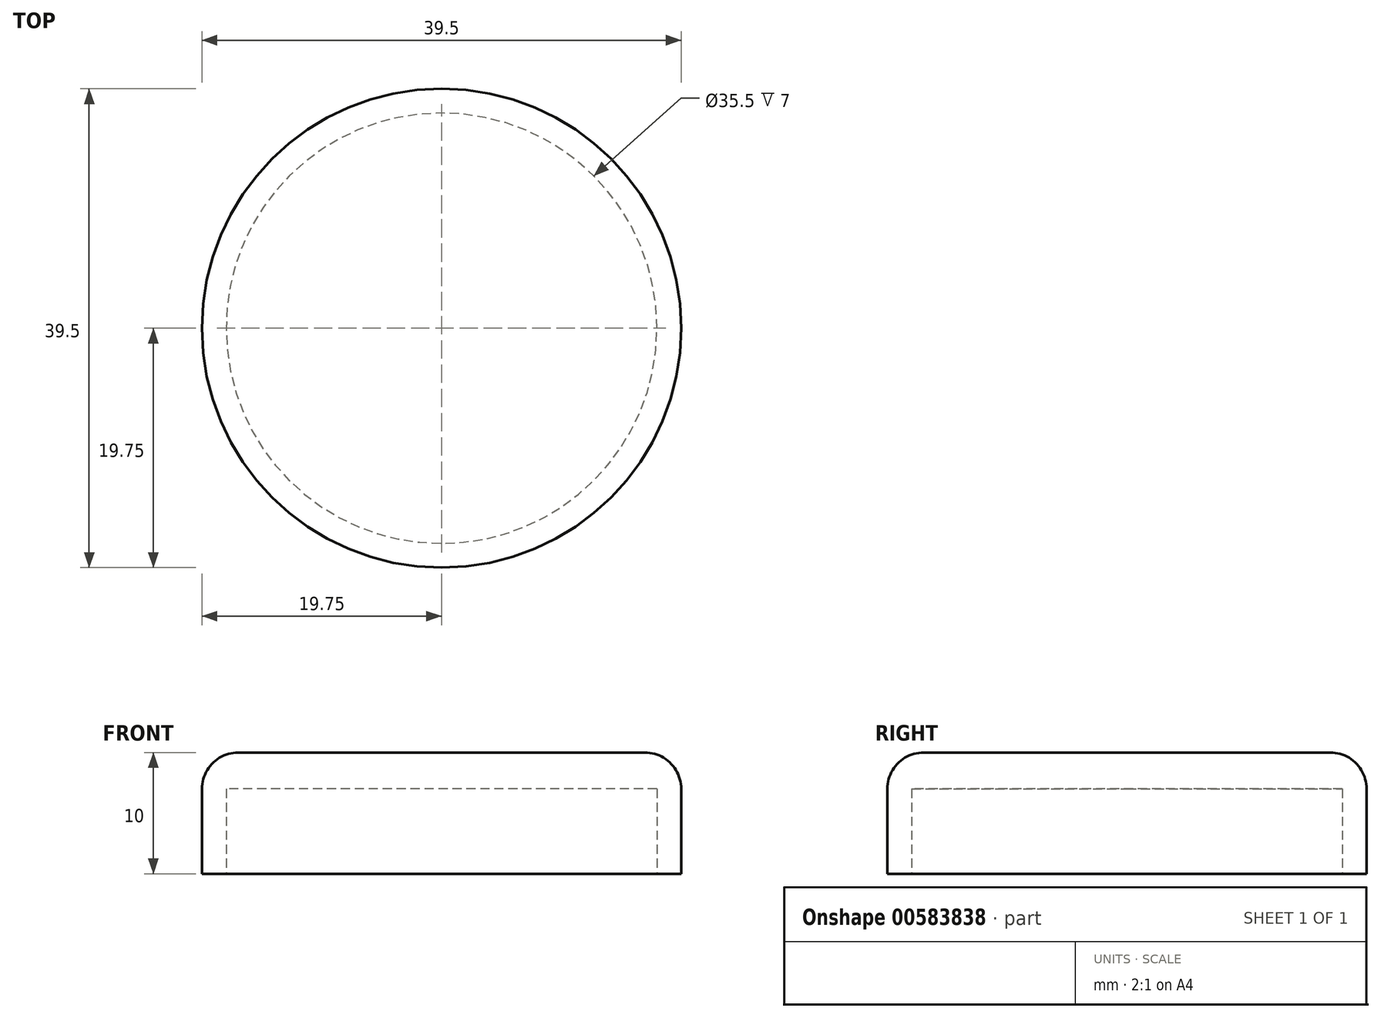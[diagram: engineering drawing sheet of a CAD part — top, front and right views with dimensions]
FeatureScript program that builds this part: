
annotation { "Feature Type Name" : "Feature", "Feature Type Description" : "" }
export const myFeature = defineFeature(function(context is Context, id is Id, definition is map)
    precondition{}
    {
        {
            assignVariable(context, id + "F0", {"name" : "OuterHeight", "anyValue" : 10});
        }
        {
            assignVariable(context, id + "F1", {"name" : "BaseDepth", "anyValue" : 3});
        }
        {
            var Q0;
            Q0=qCreatedBy(makeId("Top.planeOp"),FACE);
            var sketch = newSketch(context, id + "F2", { "sketchPlane" : qUnion([Q0])});
            skCircle(sketch, "E0", {"center": v(0, 0) * mm, "radius": 17.75 * mm});
            skCircle(sketch, "E1", {"center": v(0, 0) * mm, "radius": 19.75 * mm});
            skSolve(sketch);
        }
        {
            var Q0;
            Q0=makeQuery(id+"F2.imprint","IMPRINT",FACE,{"disambiguationData":[TD([[makeQuery(id+"F2.imprint","IMPRINT",EDGE,{"derivedFrom":sQuery(id+"F2.wireOp",EDGE,"E0")}),-1.0]])]});
            var Q1;
            Q1=makeQuery(id+"F2.imprint","IMPRINT",FACE,{"disambiguationData":[TD([[makeQuery(id+"F2.imprint","IMPRINT",EDGE,{"derivedFrom":sQuery(id+"F2.wireOp",EDGE,"E0")}),1.0]])]});
            extrude(context, id + "F3", {"entities" : qUnion([Q0, Q1]), "depth" : getVariable(context, 'OuterHeight') * mm, "offsetDistance" : 25 * mm});
        }
        {
            var Q0;
            Q0=makeQuery(id+"F2.imprint","IMPRINT",FACE,{"disambiguationData":[TD([[makeQuery(id+"F2.imprint","IMPRINT",EDGE,{"derivedFrom":sQuery(id+"F2.wireOp",EDGE,"E0")}),1.0]])]});
            extrude(context, id + "F4", {"entities" : qUnion([Q0]), "operationType" : NewBodyOperationType.REMOVE, "depth" : (getVariable(context, 'OuterHeight') - getVariable(context, 'BaseDepth')) * mm, "offsetDistance" : 25 * mm});
        }
        {
            var Q0;
            Q0=makeQuery(id+"F3.opExtrude","CAP_EDGE",EDGE,{"disambiguationData":[OSD([sQuery(id+"F2.wireOp",EDGE,"E1")])],"isStart":false});
            fillet(context, id + "F5", {"entities" : qUnion([Q0]), "radius" : getVariable(context, 'BaseDepth') * mm, "tangentPropagation" : true, "allowEdgeOverflow" : false});
        }
    });
